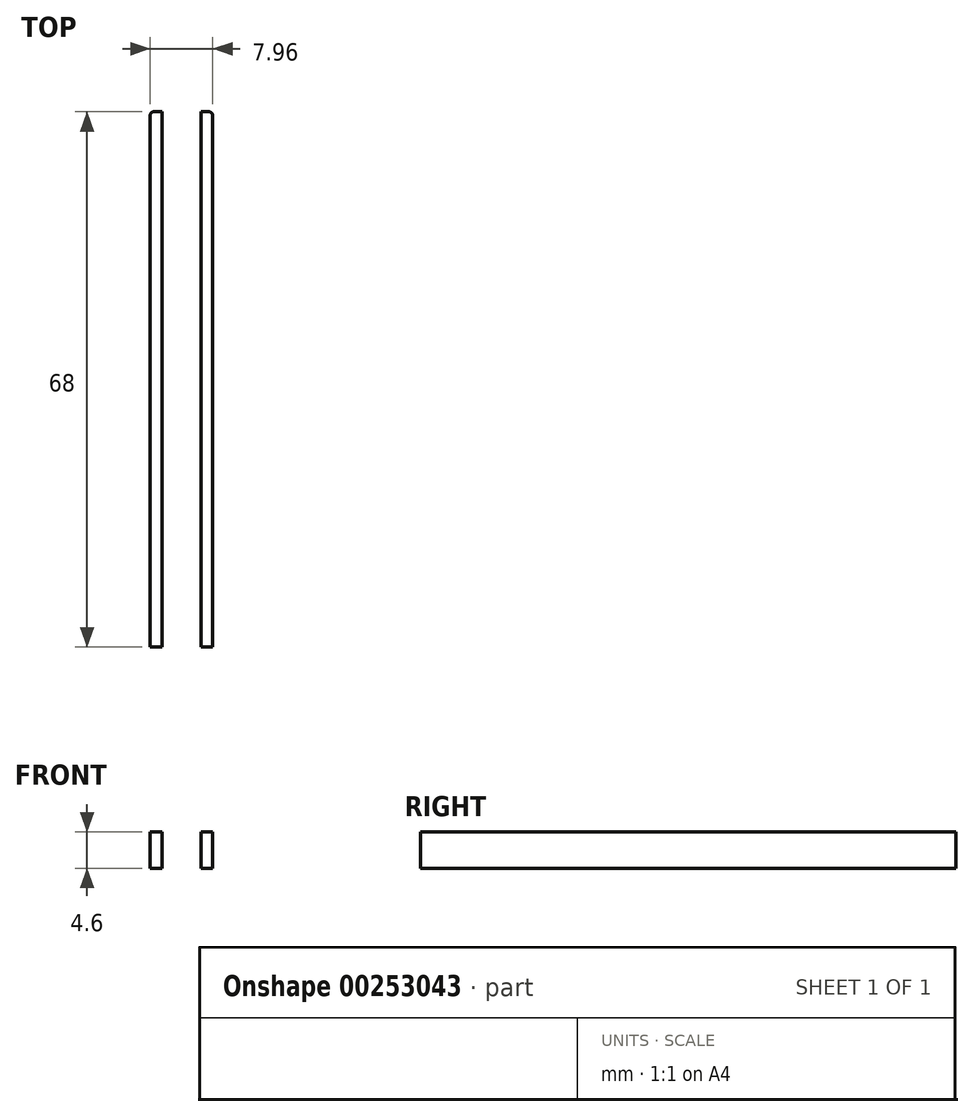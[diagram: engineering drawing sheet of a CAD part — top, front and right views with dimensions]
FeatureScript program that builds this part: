
annotation { "Feature Type Name" : "Feature", "Feature Type Description" : "" }
export const myFeature = defineFeature(function(context is Context, id is Id, definition is map)
    precondition{}
    {
        {
            var Q0;
            Q0=qCreatedBy(makeId("Top.planeOp"),FACE);
            var sketch = newSketch(context, id + "F0", { "sketchPlane" : qUnion([Q0])});
            skLineSegment(sketch, "E0.bottom", {"start": v(-1.26, 34) * mm, "end": v(-2.76, 34) * mm});
            skLineSegment(sketch, "E0.top", {"start": v(-1.26, -34) * mm, "end": v(-2.76, -34) * mm});
            skLineSegment(sketch, "E0.left", {"start": v(-1.26, 34) * mm, "end": v(-1.26, -34) * mm});
            skLineSegment(sketch, "E0.right", {"start": v(-2.76, 34) * mm, "end": v(-2.76, -34) * mm});
            skPoint(sketch, "E0.middle", {"position": v(-2.01, 0) * mm});
            skLineSegment(sketch, "E1.bottom", {"start": v(5.2, 34) * mm, "end": v(3.7, 34) * mm});
            skLineSegment(sketch, "E1.top", {"start": v(5.2, -34) * mm, "end": v(3.7, -34) * mm});
            skLineSegment(sketch, "E1.left", {"start": v(5.2, 34) * mm, "end": v(5.2, -34) * mm});
            skLineSegment(sketch, "E1.right", {"start": v(3.7, 34) * mm, "end": v(3.7, -34) * mm});
            skPoint(sketch, "E1.middle", {"position": v(4.45, 0) * mm});
            skSolve(sketch);
        }
        {
            var Q0;
            Q0 = qSketchRegion(id + "F0", true);
            extrude(context, id + "F1", {"entities" : qUnion([Q0]), "depth" : 4.6 * mm});
        }
        {
            var Q0;
            Q0=makeQuery(id+"F1.opExtrude","SWEPT_EDGE",EDGE,{"disambiguationData":[OSD([sQuery(id+"F0.wireOp",EDGE,"E0.bottom"),sQuery(id+"F0.wireOp",EDGE,"E0.right")])]});
            var Q1;
            Q1=makeQuery(id+"F1.opExtrude","SWEPT_EDGE",EDGE,{"disambiguationData":[OSD([sQuery(id+"F0.wireOp",EDGE,"E1.bottom"),sQuery(id+"F0.wireOp",EDGE,"E1.left")])]});
            fillet(context, id + "F2", {"entities" : qUnion([Q0, Q1]), "radius" : .5 * mm, "tangentPropagation" : true, "allowEdgeOverflow" : false});
        }
    });
